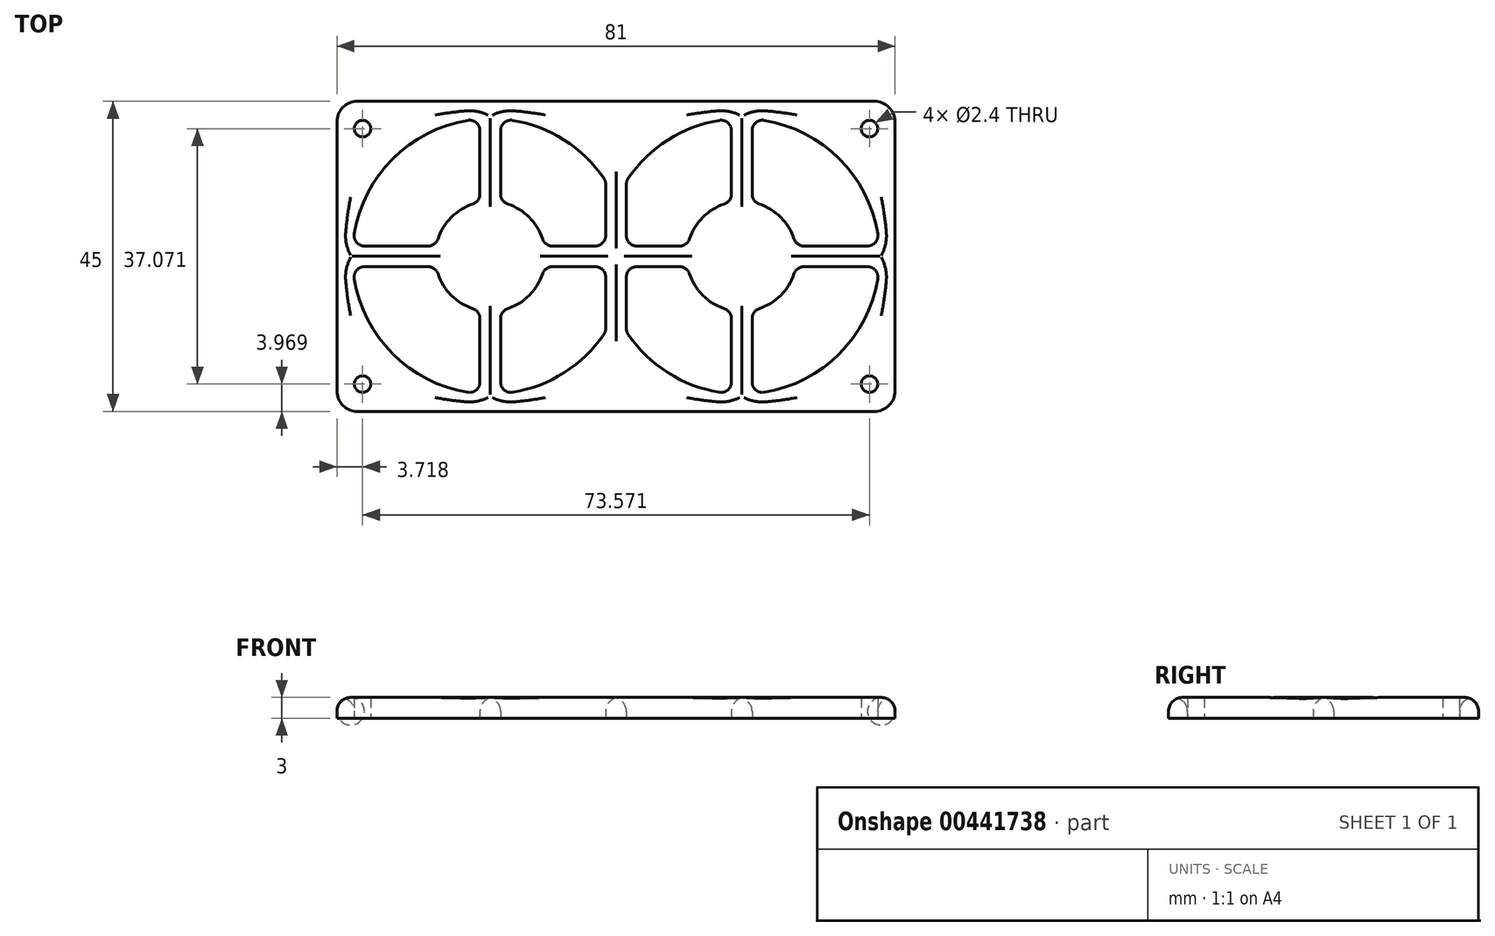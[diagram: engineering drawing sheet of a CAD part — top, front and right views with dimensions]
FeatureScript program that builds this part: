
annotation { "Feature Type Name" : "Feature", "Feature Type Description" : "" }
export const myFeature = defineFeature(function(context is Context, id is Id, definition is map)
    precondition{}
    {
        {
            var Q0;
            Q0=qCreatedBy(makeId("Top.planeOp"),FACE);
            var sketch = newSketch(context, id + "F0", { "sketchPlane" : qUnion([Q0])});
            skArc(sketch, "E0", {"start": v(-51.16, -33.68) * mm, "mid": v(-45.57, -44.58) * mm, "end": v(-34.67, -50.17) * mm});
            skArc(sketch, "E1", {"start": v(-39.02, -32.96) * mm, "mid": v(-37.08, -36.1) * mm, "end": v(-33.95, -38.03) * mm});
            skLineSegment(sketch, "E2", {"start": v(-32.93, -12.18) * mm, "end": v(-32.93, -21.42) * mm});
            skLineSegment(sketch, "E3", {"start": v(-29.93, -48.7) * mm, "end": v(-29.93, -39.45) * mm});
            skLineSegment(sketch, "E4", {"start": v(-49.68, -28.94) * mm, "end": v(-40.44, -28.94) * mm});
            skLineSegment(sketch, "E5", {"start": v(-49.68, -31.94) * mm, "end": v(-40.44, -31.94) * mm});
            skLineSegment(sketch, "E6.trimOffspring", {"start": v(-29.93, -21.42) * mm, "end": v(-29.93, -12.18) * mm});
            skLineSegment(sketch, "E7.trimOffspring", {"start": v(-22.41, -28.94) * mm, "end": v(-16.18, -28.94) * mm});
            skLineSegment(sketch, "E8.trimOffspring", {"start": v(-22.41, -31.94) * mm, "end": v(-16.18, -31.94) * mm});
            skLineSegment(sketch, "E9.trimOffspring", {"start": v(-32.93, -39.45) * mm, "end": v(-32.93, -48.7) * mm});
            skArc(sketch, "E10.trimOffspring", {"start": v(-33.95, -22.85) * mm, "mid": v(-37.08, -24.78) * mm, "end": v(-39.02, -27.9) * mm});
            skArc(sketch, "E11.trimOffspring", {"start": v(-34.67, -10.7) * mm, "mid": v(-45.57, -16.3) * mm, "end": v(-51.16, -27.2) * mm});
            skArc(sketch, "E12.trimOffspring", {"start": v(-23.84, -27.9) * mm, "mid": v(-25.77, -24.78) * mm, "end": v(-28.9, -22.85) * mm});
            skArc(sketch, "E13.trimOffspring", {"start": v(-14.94, -19.11) * mm, "mid": v(-20.7, -13.55) * mm, "end": v(-28.18, -10.7) * mm});
            skArc(sketch, "E14.trimOffspring", {"start": v(-28.9, -38.03) * mm, "mid": v(-25.77, -36.1) * mm, "end": v(-23.84, -32.96) * mm});
            skArc(sketch, "E15.trimOffspring", {"start": v(-28.18, -50.17) * mm, "mid": v(-20.7, -47.32) * mm, "end": v(-14.94, -41.76) * mm});
            skPoint(sketch, "E16.visualSharp", {"position": v(-32.93, -10.5) * mm});
            skArc(sketch, "E16.filletArc", {"start": v(-32.93, -12.18) * mm, "mid": v(-33.46, -11.04) * mm, "end": v(-34.67, -10.7) * mm});
            skPoint(sketch, "E17.visualSharp", {"position": v(-32.93, -22.58) * mm});
            skArc(sketch, "E17.filletArc", {"start": v(-33.95, -22.85) * mm, "mid": v(-33.21, -22.3) * mm, "end": v(-32.93, -21.42) * mm});
            skPoint(sketch, "E18.visualSharp", {"position": v(-51.37, -28.94) * mm});
            skArc(sketch, "E18.filletArc", {"start": v(-51.16, -27.2) * mm, "mid": v(-50.83, -28.4) * mm, "end": v(-49.68, -28.94) * mm});
            skPoint(sketch, "E19.visualSharp", {"position": v(-39.29, -28.94) * mm});
            skArc(sketch, "E19.filletArc", {"start": v(-40.44, -28.94) * mm, "mid": v(-39.56, -28.65) * mm, "end": v(-39.02, -27.9) * mm});
            skPoint(sketch, "E20.visualSharp", {"position": v(-51.37, -31.94) * mm});
            skArc(sketch, "E20.filletArc", {"start": v(-49.68, -31.94) * mm, "mid": v(-50.83, -32.47) * mm, "end": v(-51.16, -33.68) * mm});
            skPoint(sketch, "E21.visualSharp", {"position": v(-39.29, -31.94) * mm});
            skArc(sketch, "E21.filletArc", {"start": v(-39.02, -32.96) * mm, "mid": v(-39.56, -32.22) * mm, "end": v(-40.44, -31.94) * mm});
            skPoint(sketch, "E22.visualSharp", {"position": v(-32.93, -38.3) * mm});
            skArc(sketch, "E22.filletArc", {"start": v(-32.93, -39.45) * mm, "mid": v(-33.21, -38.57) * mm, "end": v(-33.95, -38.03) * mm});
            skPoint(sketch, "E23.visualSharp", {"position": v(-32.93, -50.38) * mm});
            skArc(sketch, "E23.filletArc", {"start": v(-34.67, -50.17) * mm, "mid": v(-33.46, -49.83) * mm, "end": v(-32.93, -48.7) * mm});
            skPoint(sketch, "E24.visualSharp", {"position": v(-29.93, -38.3) * mm});
            skArc(sketch, "E24.filletArc", {"start": v(-28.9, -38.03) * mm, "mid": v(-29.64, -38.57) * mm, "end": v(-29.93, -39.45) * mm});
            skPoint(sketch, "E25.visualSharp", {"position": v(-29.93, -50.38) * mm});
            skArc(sketch, "E25.filletArc", {"start": v(-29.93, -48.7) * mm, "mid": v(-29.4, -49.83) * mm, "end": v(-28.18, -50.17) * mm});
            skPoint(sketch, "E26.visualSharp", {"position": v(-23.57, -31.94) * mm});
            skArc(sketch, "E26.filletArc", {"start": v(-22.41, -31.94) * mm, "mid": v(-23.3, -32.22) * mm, "end": v(-23.84, -32.96) * mm});
            skPoint(sketch, "E27.visualSharp", {"position": v(-11.48, -31.94) * mm});
            skPoint(sketch, "E28.visualSharp", {"position": v(-11.48, -28.94) * mm});
            skPoint(sketch, "E29.visualSharp", {"position": v(-23.57, -28.94) * mm});
            skArc(sketch, "E29.filletArc", {"start": v(-23.84, -27.9) * mm, "mid": v(-23.3, -28.65) * mm, "end": v(-22.41, -28.94) * mm});
            skPoint(sketch, "E30.visualSharp", {"position": v(-29.93, -22.58) * mm});
            skArc(sketch, "E30.filletArc", {"start": v(-29.93, -21.42) * mm, "mid": v(-29.64, -22.3) * mm, "end": v(-28.9, -22.85) * mm});
            skPoint(sketch, "E31.visualSharp", {"position": v(-29.93, -10.5) * mm});
            skArc(sketch, "E31.filletArc", {"start": v(-28.18, -10.7) * mm, "mid": v(-29.4, -11.04) * mm, "end": v(-29.93, -12.18) * mm});
            skPoint(sketch, "E32.1.0.0", {"position": v(6.57, -22.58) * mm});
            skPoint(sketch, "E32.1.0.1", {"position": v(3.57, -38.3) * mm});
            skPoint(sketch, "E32.1.0.2", {"position": v(25.02, -28.94) * mm});
            skPoint(sketch, "E32.1.0.3", {"position": v(-14.87, -31.94) * mm});
            skPoint(sketch, "E32.1.0.4", {"position": v(25.02, -31.94) * mm});
            skPoint(sketch, "E32.1.0.5", {"position": v(-2.79, -28.94) * mm});
            skArc(sketch, "E32.1.0.6", {"start": v(24.8, -27.2) * mm, "mid": v(19.22, -16.3) * mm, "end": v(8.32, -10.7) * mm});
            skArc(sketch, "E32.1.0.7", {"start": v(7.6, -38.03) * mm, "mid": v(10.73, -36.1) * mm, "end": v(12.66, -32.96) * mm});
            skArc(sketch, "E32.1.0.8", {"start": v(8.32, -50.17) * mm, "mid": v(19.22, -44.58) * mm, "end": v(24.8, -33.68) * mm});
            skArc(sketch, "E32.1.0.9", {"start": v(-11.41, -41.76) * mm, "mid": v(-5.65, -47.32) * mm, "end": v(1.83, -50.17) * mm});
            skArc(sketch, "E32.1.0.10", {"start": v(-2.52, -32.96) * mm, "mid": v(-0.58, -36.1) * mm, "end": v(2.55, -38.03) * mm});
            skLineSegment(sketch, "E32.1.0.11", {"start": v(3.57, -12.18) * mm, "end": v(3.57, -21.42) * mm});
            skLineSegment(sketch, "E32.1.0.12", {"start": v(6.57, -48.7) * mm, "end": v(6.57, -39.45) * mm});
            skLineSegment(sketch, "E32.1.0.13", {"start": v(-13.18, -28.94) * mm, "end": v(-13.17, -28.94) * mm});
            skLineSegment(sketch, "E32.1.0.14", {"start": v(-13.18, -31.94) * mm, "end": v(-13.17, -31.94) * mm});
            skLineSegment(sketch, "E32.1.0.15", {"start": v(6.57, -21.42) * mm, "end": v(6.57, -12.18) * mm});
            skLineSegment(sketch, "E32.1.0.16", {"start": v(14.09, -28.94) * mm, "end": v(23.33, -28.94) * mm});
            skPoint(sketch, "E32.1.0.17", {"position": v(-14.87, -28.94) * mm});
            skLineSegment(sketch, "E32.1.0.18", {"start": v(14.09, -31.94) * mm, "end": v(23.33, -31.94) * mm});
            skPoint(sketch, "E32.1.0.19", {"position": v(12.93, -31.94) * mm});
            skLineSegment(sketch, "E32.1.0.20", {"start": v(3.57, -39.45) * mm, "end": v(3.57, -48.7) * mm});
            skArc(sketch, "E32.1.0.21", {"start": v(2.55, -22.85) * mm, "mid": v(-0.58, -24.78) * mm, "end": v(-2.52, -27.9) * mm});
            skArc(sketch, "E32.1.0.22", {"start": v(1.83, -10.7) * mm, "mid": v(-5.65, -13.55) * mm, "end": v(-11.41, -19.11) * mm});
            skPoint(sketch, "E32.1.0.23", {"position": v(3.57, -10.5) * mm});
            skArc(sketch, "E32.1.0.24", {"start": v(12.66, -27.9) * mm, "mid": v(10.73, -24.78) * mm, "end": v(7.6, -22.85) * mm});
            skPoint(sketch, "E32.1.0.25", {"position": v(6.57, -38.3) * mm});
            skPoint(sketch, "E32.1.0.26", {"position": v(6.57, -10.5) * mm});
            skPoint(sketch, "E32.1.0.27", {"position": v(3.57, -50.38) * mm});
            skPoint(sketch, "E32.1.0.28", {"position": v(12.93, -28.94) * mm});
            skPoint(sketch, "E32.1.0.29", {"position": v(-2.79, -31.94) * mm});
            skPoint(sketch, "E32.1.0.30", {"position": v(3.57, -22.58) * mm});
            skPoint(sketch, "E32.1.0.31", {"position": v(6.57, -50.38) * mm});
            skArc(sketch, "E32.1.0.32", {"start": v(24.8, -33.68) * mm, "mid": v(24.47, -32.47) * mm, "end": v(23.33, -31.94) * mm});
            skArc(sketch, "E32.1.0.33", {"start": v(1.83, -50.17) * mm, "mid": v(3.04, -49.83) * mm, "end": v(3.57, -48.7) * mm});
            skArc(sketch, "E32.1.0.35", {"start": v(3.57, -12.18) * mm, "mid": v(3.04, -11.04) * mm, "end": v(1.83, -10.7) * mm});
            skArc(sketch, "E32.1.0.36", {"start": v(23.33, -28.94) * mm, "mid": v(24.47, -28.4) * mm, "end": v(24.8, -27.2) * mm});
            skArc(sketch, "E32.1.0.37", {"start": v(7.6, -38.03) * mm, "mid": v(6.86, -38.57) * mm, "end": v(6.57, -39.45) * mm});
            skArc(sketch, "E32.1.0.38", {"start": v(6.57, -21.42) * mm, "mid": v(6.86, -22.3) * mm, "end": v(7.6, -22.85) * mm});
            skArc(sketch, "E32.1.0.39", {"start": v(-2.52, -32.96) * mm, "mid": v(-3.06, -32.22) * mm, "end": v(-3.94, -31.94) * mm});
            skArc(sketch, "E32.1.0.40", {"start": v(6.57, -48.7) * mm, "mid": v(7.1, -49.83) * mm, "end": v(8.32, -50.17) * mm});
            skArc(sketch, "E32.1.0.41", {"start": v(8.32, -10.7) * mm, "mid": v(7.1, -11.04) * mm, "end": v(6.57, -12.18) * mm});
            skArc(sketch, "E32.1.0.43", {"start": v(-3.94, -28.94) * mm, "mid": v(-3.06, -28.65) * mm, "end": v(-2.52, -27.9) * mm});
            skArc(sketch, "E32.1.0.44", {"start": v(12.66, -27.9) * mm, "mid": v(13.2, -28.65) * mm, "end": v(14.09, -28.94) * mm});
            skArc(sketch, "E32.1.0.45", {"start": v(2.55, -22.85) * mm, "mid": v(3.29, -22.3) * mm, "end": v(3.57, -21.42) * mm});
            skArc(sketch, "E32.1.0.46", {"start": v(3.57, -39.45) * mm, "mid": v(3.29, -38.57) * mm, "end": v(2.55, -38.03) * mm});
            skArc(sketch, "E32.1.0.47", {"start": v(14.09, -31.94) * mm, "mid": v(13.2, -32.22) * mm, "end": v(12.66, -32.96) * mm});
            skLineSegment(sketch, "E32.direction1", {"start": v(-34.67, -50.17) * mm, "end": v(1.83, -50.17) * mm, "construction": true});
            skLineSegment(sketch, "E33.left", {"start": v(-14.68, -19.96) * mm, "end": v(-14.68, -27.44) * mm});
            skLineSegment(sketch, "E33.right", {"start": v(-11.68, -19.96) * mm, "end": v(-11.68, -27.44) * mm});
            skLineSegment(sketch, "E34.trimOffspring", {"start": v(-10.18, -28.94) * mm, "end": v(-3.94, -28.94) * mm});
            skLineSegment(sketch, "E35.trimOffspring", {"start": v(-10.18, -31.94) * mm, "end": v(-3.94, -31.94) * mm});
            skLineSegment(sketch, "E36.trimOffspring", {"start": v(-14.68, -33.44) * mm, "end": v(-14.68, -40.9) * mm});
            skLineSegment(sketch, "E37.trimOffspring", {"start": v(-11.68, -33.44) * mm, "end": v(-11.68, -40.9) * mm});
            skPoint(sketch, "E38.visualSharp", {"position": v(-14.68, -28.94) * mm});
            skArc(sketch, "E38.filletArc", {"start": v(-16.18, -28.94) * mm, "mid": v(-15.12, -28.5) * mm, "end": v(-14.68, -27.44) * mm});
            skPoint(sketch, "E39.visualSharp", {"position": v(-14.68, -31.94) * mm});
            skArc(sketch, "E39.filletArc", {"start": v(-14.68, -33.44) * mm, "mid": v(-15.12, -32.38) * mm, "end": v(-16.18, -31.94) * mm});
            skPoint(sketch, "E40.visualSharp", {"position": v(-11.68, -28.94) * mm});
            skArc(sketch, "E40.filletArc", {"start": v(-11.68, -27.44) * mm, "mid": v(-11.24, -28.5) * mm, "end": v(-10.18, -28.94) * mm});
            skPoint(sketch, "E41.visualSharp", {"position": v(-11.68, -31.94) * mm});
            skArc(sketch, "E41.filletArc", {"start": v(-10.18, -31.94) * mm, "mid": v(-11.24, -32.38) * mm, "end": v(-11.68, -33.44) * mm});
            skPoint(sketch, "E42.visualSharp", {"position": v(-11.68, -19.5) * mm});
            skArc(sketch, "E42.filletArc", {"start": v(-11.41, -19.11) * mm, "mid": v(-11.6, -19.52) * mm, "end": v(-11.68, -19.96) * mm});
            skPoint(sketch, "E43.visualSharp", {"position": v(-14.68, -19.5) * mm});
            skArc(sketch, "E43.filletArc", {"start": v(-14.68, -19.96) * mm, "mid": v(-14.74, -19.52) * mm, "end": v(-14.94, -19.11) * mm});
            skPoint(sketch, "E44.visualSharp", {"position": v(-14.68, -41.36) * mm});
            skArc(sketch, "E44.filletArc", {"start": v(-14.94, -41.76) * mm, "mid": v(-14.74, -41.35) * mm, "end": v(-14.68, -40.9) * mm});
            skPoint(sketch, "E45.visualSharp", {"position": v(-11.68, -41.36) * mm});
            skArc(sketch, "E45.filletArc", {"start": v(-11.68, -40.9) * mm, "mid": v(-11.6, -41.35) * mm, "end": v(-11.41, -41.76) * mm});
            skCircle(sketch, "E46", {"center": v(-49.96, -11.9) * mm, "radius": 1.2 * mm});
            skCircle(sketch, "E47", {"center": v(-49.96, -48.97) * mm, "radius": 1.2 * mm});
            skCircle(sketch, "E48", {"center": v(23.6, -11.9) * mm, "radius": 1.2 * mm});
            skCircle(sketch, "E49", {"center": v(23.6, -48.97) * mm, "radius": 1.2 * mm});
            skLineSegment(sketch, "E50.bottom", {"start": v(-50.68, -7.94) * mm, "end": v(24.32, -7.94) * mm});
            skLineSegment(sketch, "E50.top", {"start": v(-50.68, -52.94) * mm, "end": v(24.32, -52.94) * mm});
            skLineSegment(sketch, "E50.left", {"start": v(-53.68, -10.94) * mm, "end": v(-53.68, -49.94) * mm});
            skLineSegment(sketch, "E50.right", {"start": v(27.32, -10.94) * mm, "end": v(27.32, -49.94) * mm});
            skPoint(sketch, "E51.visualSharp", {"position": v(-53.68, -7.94) * mm});
            skArc(sketch, "E51.filletArc", {"start": v(-50.68, -7.94) * mm, "mid": v(-52.8, -8.81) * mm, "end": v(-53.68, -10.94) * mm});
            skPoint(sketch, "E52.visualSharp", {"position": v(27.32, -7.94) * mm});
            skArc(sketch, "E52.filletArc", {"start": v(27.32, -10.94) * mm, "mid": v(26.44, -8.81) * mm, "end": v(24.32, -7.94) * mm});
            skPoint(sketch, "E53.visualSharp", {"position": v(27.32, -52.94) * mm});
            skArc(sketch, "E53.filletArc", {"start": v(24.32, -52.94) * mm, "mid": v(26.44, -52.06) * mm, "end": v(27.32, -49.94) * mm});
            skPoint(sketch, "E54.visualSharp", {"position": v(-53.68, -52.94) * mm});
            skArc(sketch, "E54.filletArc", {"start": v(-53.68, -49.94) * mm, "mid": v(-52.8, -52.06) * mm, "end": v(-50.68, -52.94) * mm});
            skSolve(sketch);
        }
        {
            var Q0;
            Q0=makeQuery(id+"F0.imprint","IMPRINT",FACE,{"disambiguationData":[TD([[makeQuery(id+"F0.imprint","IMPRINT",EDGE,{"derivedFrom":sQuery(id+"F0.wireOp",EDGE,"E0")}),-1.0]])]});
            extrude(context, id + "F1", {"entities" : qUnion([Q0]), "depth" : 3 * mm});
        }
        {
            var Q0;
            Q0=makeQuery(id+"F1.opExtrude","CAP_EDGE",EDGE,{"disambiguationData":[OSD([sQuery(id+"F0.wireOp",EDGE,"E32.1.0.6")])],"isStart":false});
            var Q1;
            Q1=makeQuery(id+"F1.opExtrude","CAP_EDGE",EDGE,{"disambiguationData":[OSD([sQuery(id+"F0.wireOp",EDGE,"E32.1.0.11")])],"isStart":false});
            var Q2;
            Q2=makeQuery(id+"F1.opExtrude","CAP_EDGE",EDGE,{"disambiguationData":[OSD([sQuery(id+"F0.wireOp",EDGE,"E32.1.0.10")])],"isStart":false});
            var Q3;
            Q3=makeQuery(id+"F1.opExtrude","CAP_EDGE",EDGE,{"disambiguationData":[OSD([sQuery(id+"F0.wireOp",EDGE,"E32.1.0.7")])],"isStart":false});
            var Q4;
            Q4=makeQuery(id+"F1.opExtrude","CAP_EDGE",EDGE,{"disambiguationData":[OSD([sQuery(id+"F0.wireOp",EDGE,"E15.trimOffspring")])],"isStart":false});
            var Q5;
            Q5=makeQuery(id+"F1.opExtrude","CAP_EDGE",EDGE,{"disambiguationData":[OSD([sQuery(id+"F0.wireOp",EDGE,"E33.left")])],"isStart":false});
            var Q6;
            Q6=makeQuery(id+"F1.opExtrude","CAP_EDGE",EDGE,{"disambiguationData":[OSD([sQuery(id+"F0.wireOp",EDGE,"E10.trimOffspring")])],"isStart":false});
            var Q7;
            Q7=makeQuery(id+"F1.opExtrude","CAP_EDGE",EDGE,{"disambiguationData":[OSD([sQuery(id+"F0.wireOp",EDGE,"E1")])],"isStart":false});
            var Q8;
            Q8=makeQuery(id+"F1.opExtrude","CAP_EDGE",EDGE,{"disambiguationData":[OSD([sQuery(id+"F0.wireOp",EDGE,"E50.left")])],"isStart":false});
            fillet(context, id + "F2", {"entities" : qUnion([Q0, Q1, Q2, Q3, Q4, Q5, Q6, Q7, Q8]), "radius" : 2 * mm, "tangentPropagation" : true, "allowEdgeOverflow" : false});
        }
    });
